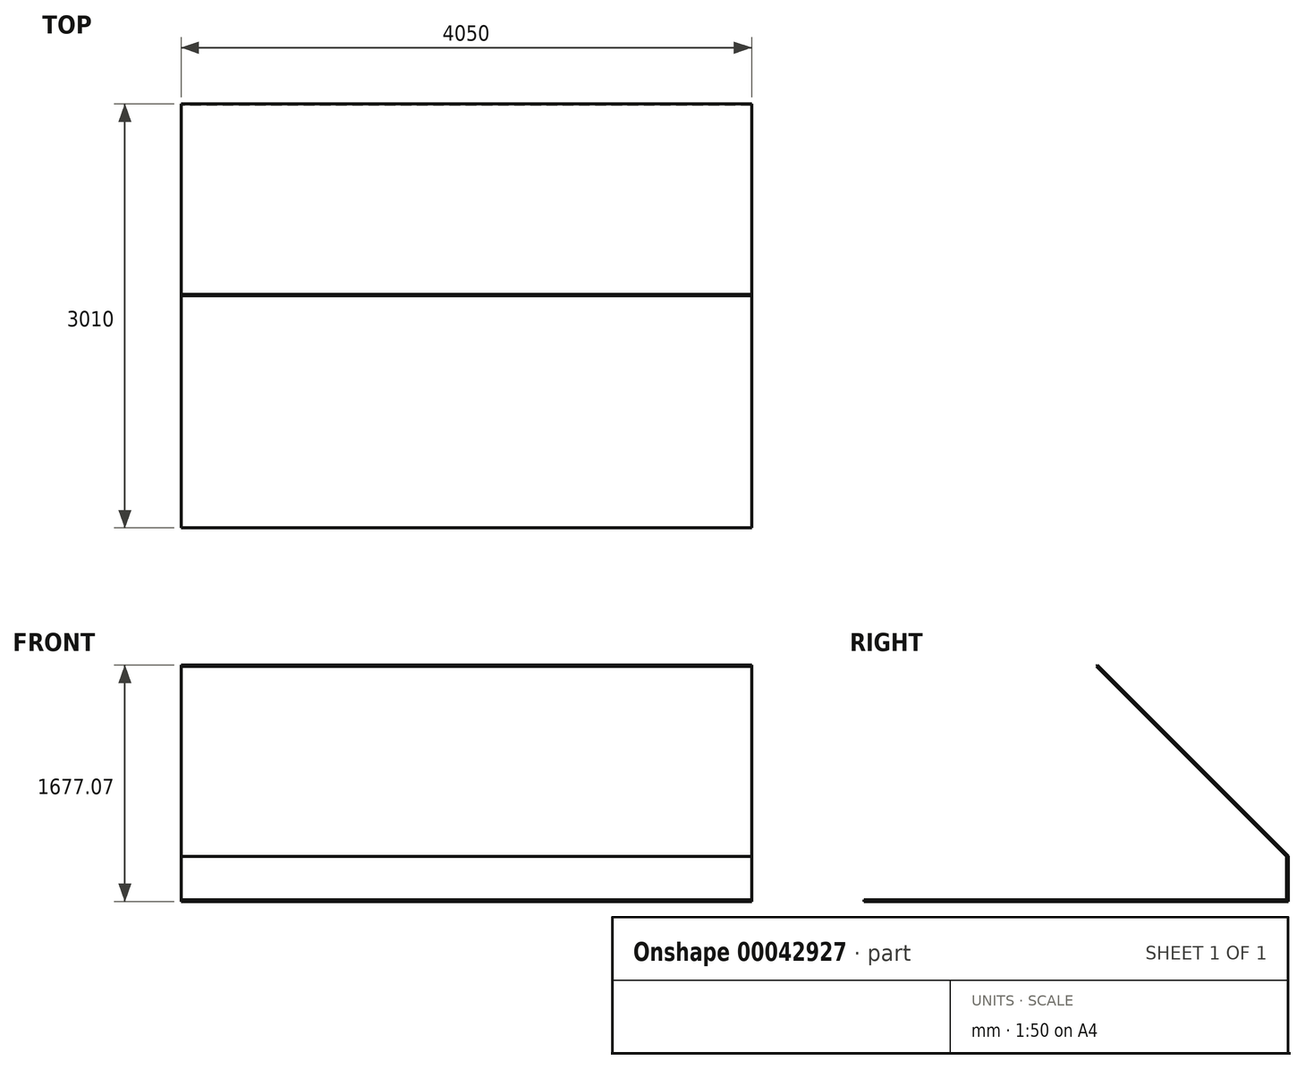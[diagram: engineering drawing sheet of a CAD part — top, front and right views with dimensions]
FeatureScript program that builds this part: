
annotation { "Feature Type Name" : "Feature", "Feature Type Description" : "" }
export const myFeature = defineFeature(function(context is Context, id is Id, definition is map)
    precondition{}
    {
        {
            var Q0;
            Q0=qCreatedBy(makeId("Right.planeOp"),FACE);
            var sketch = newSketch(context, id + "F0", { "sketchPlane" : qUnion([Q0])});
            skLineSegment(sketch, "E0", {"start": v(0, 0) * mm, "end": v(-3000, 0) * mm});
            skLineSegment(sketch, "E1", {"start": v(-3000, 0) * mm, "end": v(-3000, -10) * mm});
            skLineSegment(sketch, "E2", {"start": v(-3000, -10) * mm, "end": v(10, -10) * mm});
            skLineSegment(sketch, "E3", {"start": v(10, -10) * mm, "end": v(10, 314.14) * mm});
            skLineSegment(sketch, "E4", {"start": v(10, 314.14) * mm, "end": v(-1342.93, 1667.07) * mm});
            skLineSegment(sketch, "E5", {"start": v(-1342.93, 1667.07) * mm, "end": v(-1350, 1660) * mm});
            skLineSegment(sketch, "E6", {"start": v(-1350, 1660) * mm, "end": v(0, 310) * mm});
            skLineSegment(sketch, "E7", {"start": v(0, 310) * mm, "end": v(0, 0) * mm});
            skSolve(sketch);
        }
        {
            var Q0;
            Q0 = qSketchRegion(id + "F0", true);
            extrude(context, id + "F1", {"entities" : qUnion([Q0]), "depth" : 4050 * mm});
        }
    });
